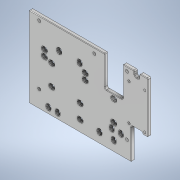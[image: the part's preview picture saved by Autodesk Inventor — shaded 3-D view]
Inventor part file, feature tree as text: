
AUTODESK INVENTOR PART (.ipt)
format: ipt  version: 2021 (Build 250183000, 183)  size: 776,192 bytes
history: native  units: mm
features: sketch x12, extrude x11, fillet x7, chamfer x1, projected_geometry x1
ambient origin geometry x8: Origin, YZ Plane, XZ Plane, XY Plane, X Axis, Y Axis, Z Axis, Center Point
bodies: Solid1 (feature_tree)
feature tree (32):
  extrude  "Extrusion1"  Depth=79.0mm
  extrude  "Extrusion2"  Depth=3.0mm
  fillet  "Fillet1"  Radius=3.0mm
  extrude  "Extrusion3"  Depth=4.0mm
  extrude  "Extrusion4"  Depth=4.0mm
  extrude  "Extrusion5"  Depth=2.0mm TaperAngle=0.0deg
  extrude  "Extrusion6"  Depth=4.0mm
  fillet  "Fillet2"  Radius=4.0mm
  sketch  "Sketch7"  dims[d18=4.0mm d19=4.0mm]
  fillet  "Fillet3"  Radius=4.0mm
  fillet  "Fillet4"  Radius=4.0mm
  extrude  "Extrusion7"  Depth=4.0mm
  extrude  "Extrusion8"  Depth=4.0mm
  fillet  "Fillet5"  Radius=4.0mm
  extrude  "Extrusion9"  Depth=5.0mm
  extrude  "Extrusion10"  Depth=5.0mm
  fillet  "Fillet6"  Radius=5.0mm
  extrude  "Extrusion11"  Depth=5.0mm
  fillet  "Fillet7"  Radius=5.0mm
  chamfer  "Chamfer1"  [1 undecoded]
  sketch  "Sketch1"  dims[d0=100.0mm d1=79.0mm]
  sketch  "Sketch2"  dims[d2=3.0mm d3=0.0mm d4=3.0mm d5=3.0mm]
  sketch  "Sketch3"  dims[d6=86.0mm d7=4.0mm]
  sketch  "Sketch4"  dims[d8=4.0mm d9=4.0mm]
  sketch  "Sketch5"  dims[d10=33.0mm d11=2.0mm d12=0.0mm]
  sketch  "Sketch6"  dims[d13=0.6mm d14=4.0mm d15=4.0mm d16=4.0mm d17=4.0mm]
  projected_geometry  "Projected Loop1"
  sketch  "Sketch8"  dims[d20=4.0mm d21=4.0mm d23=4.0mm]
  sketch  "Sketch9"  dims[d24=5.0mm d25=5.0mm]
  sketch  "Sketch10"  dims[d26=5.0mm d27=5.0mm d29=5.0mm]
  sketch  "Sketch11"  dims[d30=5.0mm d31=5.0mm d32=5.0mm]
  sketch  "Sketch12"  dims[d33=5.0mm d34=0.0mm d35=20.0mm d36=20.0mm d37=14.0mm d38=14.0mm d40=17.0mm d41=10.0mm d42=25.0mm d43=50.0mm d44=34.0mm d45=4.0mm d46=5.0mm d47=20.0mm d48=0.0mm d49=0.0mm d50=17.0mm d51=0.0mm d52=0.0mm d54=4.0mm d55=5.0mm d56=4.0mm d57=5.0mm d60=4.0mm d61=5.0mm d62=2.0mm d63=5.0mm d64=0.0mm d65=5.0mm d66=19.0mm d67=6.0mm d72=4.0mm d73=5.0mm d74=4.0mm d75=5.0mm d76=0.0mm d77=5.0mm d78=2.0mm d79=5.0mm d80=2.0mm d81=5.0mm d82=10.022273mm d83=2.022273mm d84=4.0mm d85=0.0mm d86=0.0mm d87=5.0mm d88=4.0mm d89=4.0mm d90=4.0mm d91=5.0mm d92=5.0mm d93=6.0mm d98=3.5mm d102=26.0mm d103=15.0mm d105=4.0mm d106=4.0mm d107=5.0mm d108=5.0mm d109=6.0mm d116=2.0mm d117=5.0mm d121=0.0mm d122=45.0mm d123=0.0mm d124=0.0mm d125=20.0mm d126=29.5mm d127=30.0mm d128=8.0mm d129=18.0mm d130=0.0mm d131=0.0mm d132=0.6mm d133=1.75mm d134=1.75mm d135=1.75mm d136=3.0mm d137=5.0mm d138=10.0mm d139=10.0mm d140=0.0mm d141=0.5mm d142=2.0mm d143=45.0deg d144=24.4mm d146=50.0mm d147=10.0mm d148=0.0mm d149=1.0mm d150=20.0mm d151=13.1mm d152=33.3mm d153=2.3mm d154=2.3mm d155=2.3mm d156=2.3mm d157=15.4mm d160=10.0mm d161=17.8mm d163=20.0mm d164=40.0mm d165=35.6mm d166=3.0mm d167=6.0mm d168=3.0mm d169=10.0mm d170=0.0mm d171=2.0mm d172=9.0mm d174=13.1mm d176=10.0mm d177=0.0mm d178=2.0mm d179=1.0mm d180=5.0mm d182=5.0mm d183=0.0mm d184=0.0mm d185=15.4mm d186=5.2mm d187=1.0mm d188=2.0mm d189=2.0mm d190=2.0mm]
note: 1 required parameter value undecoded (feature->parameter linkage not recoverable at this tier; creation-order binding heuristic only, values carry confidence <= 0.55)
